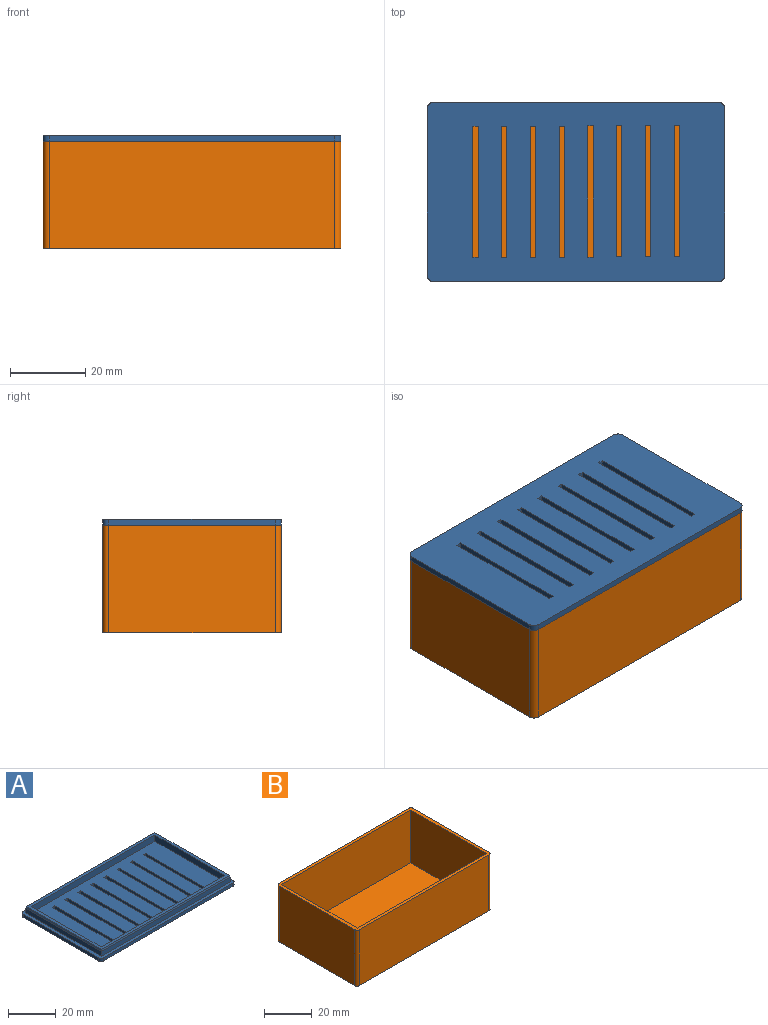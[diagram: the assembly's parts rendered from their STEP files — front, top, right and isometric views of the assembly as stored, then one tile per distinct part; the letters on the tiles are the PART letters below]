
ASSEMBLY  parts=2 mates=1
PART A: 56 faces, bbox 79.4x47.6x4.8 mm
  f0: plane 73.03x41.28mm, normal (0,0,1), area 2624.3mm2, adj f7,f8,f9,f14,f24,f25,f26,f27
  f1: plane 79.38x47.63mm, normal (0,0,1), area 391mm2, adj f2,f3,f4,f5,f10,f11,f12,f13
  f2: plane 76.2x1.59mm, normal (0,-1,0), area 121mm2, adj f1,f6,f16,f19
  f3: plane 44.45x1.59mm, normal (1,0,0), area 70.6mm2, adj f1,f6,f16,f17
  f4: plane 76.2x1.59mm, normal (0,1,0), area 121mm2, adj f1,f6,f17,f18
  f5: plane 44.45x1.59mm, normal (-1,0,0), area 70.6mm2, adj f1,f6,f18,f19
  f6: plane 79.38x47.63mm, normal (0,0,-1), area 3388.3mm2, adj f2,f3,f4,f5,f16,f17,f18,f19
  f7: plane 73.03x3.18mm, normal (0,-1,0), area 231.9mm2, adj f0,f8,f14,f15
  f8: plane 41.28x3.18mm, normal (-1,0,0), area 131mm2, adj f0,f7,f9,f15
  f9: plane 73.03x3.18mm, normal (0,1,0), area 231.9mm2, adj f0,f8,f14,f15
  f10: plane 44.45x2.38mm, normal (1,0,0), area 105.8mm2, adj f1,f11,f13,f20
  f11: plane 76.2x2.38mm, normal (0,1,0), area 181.5mm2, adj f1,f10,f12,f21
  f12: plane 44.45x2.38mm, normal (-1,0,0), area 105.8mm2, adj f1,f11,f13,f23
  f13: plane 76.2x2.38mm, normal (0,-1,0), area 181.5mm2, adj f1,f10,f12,f22
  f14: plane 41.28x3.18mm, normal (1,0,0), area 131mm2, adj f0,f7,f9,f15
  f15: plane 75.69x43.94mm, normal (0,0,1), area 312mm2, adj f7,f8,f9,f14,f20,f21,f22,f23
  f16: cylinder r=1.59mm len=1.59mm, axis (0,0,-1), area 4mm2, adj f1,f2,f3,f6
  f17: cylinder r=1.59mm len=1.59mm, axis (0,0,1), area 4mm2, adj f1,f3,f4,f6
  f18: cylinder r=1.59mm len=1.59mm, axis (0,0,-1), area 4mm2, adj f1,f4,f5,f6
  f19: cylinder r=1.59mm len=1.59mm, axis (0,0,1), area 4mm2, adj f1,f2,f5,f6
  f20: plane 44.45x0.79mm, normal (0.95,0,0.3), area 36.8mm2, adj f10,f15,f21,f22
  f21: plane 76.2x0.79mm, normal (0,0.95,0.3), area 63.3mm2, adj f11,f15,f20,f23
  f22: plane 76.2x0.79mm, normal (0,-0.95,0.3), area 63.3mm2, adj f13,f15,f20,f23
  f23: plane 44.45x0.79mm, normal (-0.95,0,0.3), area 36.8mm2, adj f12,f15,f21,f22
  f24: plane 34.93x1.59mm, normal (1,0,0), area 55.4mm2, adj f0,f6,f25,f26
  f25: plane 1.59x1.4mm, normal (0,-1,0), area 2.2mm2, adj f0,f6,f24,f27
  f26: plane 1.59x1.4mm, normal (0,1,0), area 2.2mm2, adj f0,f6,f24,f27
  f27: plane 34.93x1.59mm, normal (-1,0,0), area 55.4mm2, adj f0,f6,f25,f26
  f28: plane 34.93x1.59mm, normal (1,0,0), area 55.4mm2, adj f0,f6,f29,f30
  f29: plane 1.59x1.4mm, normal (0,-1,0), area 2.2mm2, adj f0,f6,f28,f31
  f30: plane 1.59x1.4mm, normal (0,1,0), area 2.2mm2, adj f0,f6,f28,f31
  f31: plane 34.93x1.59mm, normal (-1,0,0), area 55.4mm2, adj f0,f6,f29,f30
  f32: plane 34.93x1.59mm, normal (1,0,0), area 55.4mm2, adj f0,f6,f33,f34
  f33: plane 1.59x1.4mm, normal (0,-1,0), area 2.2mm2, adj f0,f6,f32,f35
  f34: plane 1.59x1.4mm, normal (0,1,0), area 2.2mm2, adj f0,f6,f32,f35
  f35: plane 34.93x1.59mm, normal (-1,0,0), area 55.4mm2, adj f0,f6,f33,f34
  f36: plane 34.93x1.59mm, normal (1,0,0), area 55.4mm2, adj f0,f6,f37,f38
  f37: plane 1.59x1.4mm, normal (0,-1,0), area 2.2mm2, adj f0,f6,f36,f39
  f38: plane 1.59x1.4mm, normal (0,1,0), area 2.2mm2, adj f0,f6,f36,f39
  f39: plane 34.93x1.59mm, normal (-1,0,0), area 55.4mm2, adj f0,f6,f37,f38
  f40: plane 34.93x1.59mm, normal (1,0,0), area 55.4mm2, adj f0,f6,f41,f42
  f41: plane 1.59x1.4mm, normal (0,-1,0), area 2.2mm2, adj f0,f6,f40,f43
  f42: plane 1.59x1.4mm, normal (0,1,0), area 2.2mm2, adj f0,f6,f40,f43
  f43: plane 34.93x1.59mm, normal (-1,0,0), area 55.4mm2, adj f0,f6,f41,f42
  f44: plane 34.93x1.59mm, normal (1,0,0), area 55.4mm2, adj f0,f6,f45,f46
  f45: plane 1.59x1.4mm, normal (0,-1,0), area 2.2mm2, adj f0,f6,f44,f47
  f46: plane 1.59x1.4mm, normal (0,1,0), area 2.2mm2, adj f0,f6,f44,f47
  f47: plane 34.93x1.59mm, normal (-1,0,0), area 55.4mm2, adj f0,f6,f45,f46
  f48: plane 34.93x1.59mm, normal (1,0,0), area 55.4mm2, adj f0,f6,f49,f50
  f49: plane 1.59x1.4mm, normal (0,-1,0), area 2.2mm2, adj f0,f6,f48,f51
  f50: plane 1.59x1.4mm, normal (0,1,0), area 2.2mm2, adj f0,f6,f48,f51
  f51: plane 34.93x1.59mm, normal (-1,0,0), area 55.4mm2, adj f0,f6,f49,f50
  f52: plane 34.93x1.59mm, normal (1,0,0), area 55.4mm2, adj f0,f6,f53,f54
  f53: plane 1.59x1.4mm, normal (0,-1,0), area 2.2mm2, adj f0,f6,f52,f55
  f54: plane 1.59x1.4mm, normal (0,1,0), area 2.2mm2, adj f0,f6,f52,f55
  f55: plane 34.93x1.59mm, normal (-1,0,0), area 55.4mm2, adj f0,f6,f53,f54
PART B: 15 faces, bbox 79.4x47.6x28.6 mm
  f0: plane 76.2x28.58mm, normal (0,-1,0), area 2177.4mm2, adj f4,f9,f11,f14
  f1: plane 44.45x28.58mm, normal (1,0,0), area 1270.2mm2, adj f4,f9,f11,f12
  f2: plane 76.2x28.58mm, normal (0,1,0), area 2177.4mm2, adj f4,f9,f12,f13
  f3: plane 44.45x28.58mm, normal (-1,0,0), area 1270.2mm2, adj f4,f9,f13,f14
  f4: plane 79.38x47.63mm, normal (0,0,-1), area 3778.1mm2, adj f0,f1,f2,f3,f11,f12,f13,f14
  f5: plane 76.2x26.99mm, normal (0,-1,0), area 2056.4mm2, adj f6,f8,f9,f10
  f6: plane 44.45x26.99mm, normal (-1,0,0), area 1199.6mm2, adj f5,f7,f9,f10
  f7: plane 76.2x26.99mm, normal (0,1,0), area 2056.4mm2, adj f6,f8,f9,f10
  f8: plane 44.45x26.99mm, normal (1,0,0), area 1199.6mm2, adj f5,f7,f9,f10
  f9: plane 79.38x47.63mm, normal (0,0,1), area 391mm2, adj f0,f1,f2,f3,f5,f6,f7,f8
  f10: plane 76.2x44.45mm, normal (0,0,1), area 3387.1mm2, adj f5,f6,f7,f8
  f11: cylinder r=1.59mm len=28.58mm, axis (0,0,-1), area 71.3mm2, adj f0,f1,f4,f9
  f12: cylinder r=1.59mm len=28.58mm, axis (0,0,1), area 71.3mm2, adj f1,f2,f4,f9
  f13: cylinder r=1.59mm len=28.58mm, axis (0,0,-1), area 71.3mm2, adj f2,f3,f4,f9
  f14: cylinder r=1.59mm len=28.58mm, axis (0,0,1), area 71.3mm2, adj f0,f3,f4,f9
PLACE A rot(axis=(1,0,0),180deg) t=(0,56.35,26.99)mm
PLACE B at identity fixed
MATE slider A.f1 <-> B.f9  axis (0,0,-1) through (-38.1,0,26.99)mm
